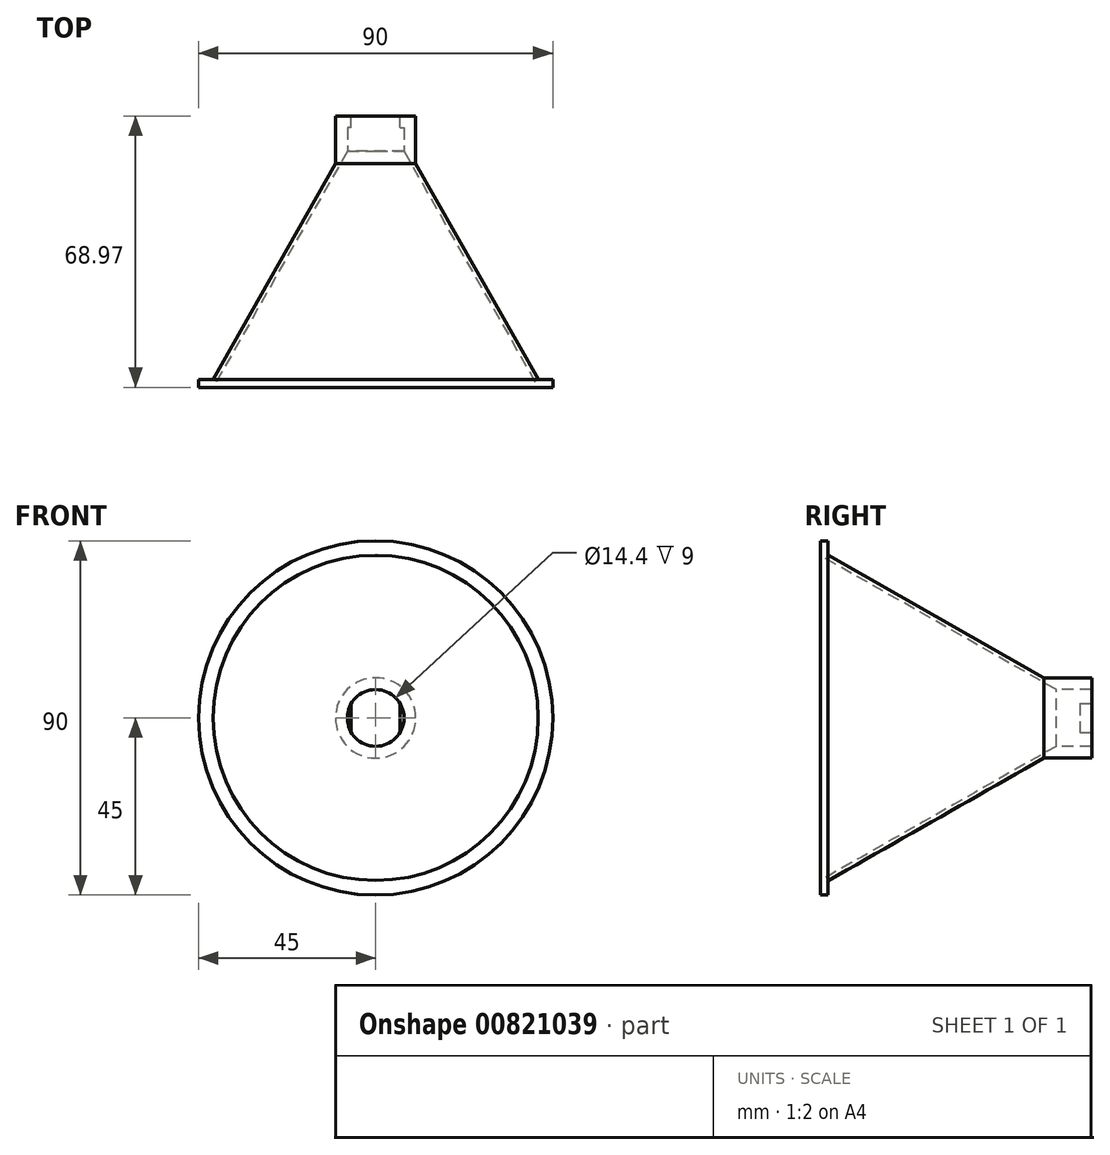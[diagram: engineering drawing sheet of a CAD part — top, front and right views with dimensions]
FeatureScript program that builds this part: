
annotation { "Feature Type Name" : "Feature", "Feature Type Description" : "" }
export const myFeature = defineFeature(function(context is Context, id is Id, definition is map)
    precondition{}
    {
        {
            var Q0;
            Q0=qCreatedBy(makeId("Top.planeOp"),FACE);
            var sketch = newSketch(context, id + "F0", { "sketchPlane" : qUnion([Q0])});
            skLineSegment(sketch, "E0", {"start": v(0, 0) * mm, "end": v(-42.5, 0) * mm});
            skLineSegment(sketch, "E1", {"start": v(0, 0) * mm, "end": v(0, 73.6) * mm});
            skLineSegment(sketch, "E2", {"start": v(0, 0) * mm, "end": v(-8.4, 0) * mm});
            skLineSegment(sketch, "E3", {"start": v(-8.4, 59.97) * mm, "end": v(0, 59.97) * mm});
            skLineSegment(sketch, "E4", {"start": v(0, 59.97) * mm, "end": v(-7.2, 59.97) * mm});
            skLineSegment(sketch, "E5", {"start": v(-8.4, 59.97) * mm, "end": v(-42.5, 0) * mm});
            skLineSegment(sketch, "E6", {"start": v(-7.2, 59.97) * mm, "end": v(-41.3, 0) * mm});
            skLineSegment(sketch, "E7", {"start": v(-7.2, 59.97) * mm, "end": v(-7.2, 68.97) * mm});
            skLineSegment(sketch, "E8", {"start": v(-7.2, 68.97) * mm, "end": v(-10.2, 68.97) * mm});
            skLineSegment(sketch, "E9", {"start": v(-10.2, 68.97) * mm, "end": v(-10.2, 59.97) * mm});
            skLineSegment(sketch, "E10", {"start": v(-10.2, 59.97) * mm, "end": v(-7.2, 59.97) * mm});
            skLineSegment(sketch, "E11", {"start": v(-10.2, 59.97) * mm, "end": v(-10.2, 56.8) * mm});
            skLineSegment(sketch, "E12", {"start": v(0, 0) * mm, "end": v(0, 2) * mm});
            skLineSegment(sketch, "E13", {"start": v(0, 2) * mm, "end": v(-45, 2) * mm});
            skLineSegment(sketch, "E14", {"start": v(-45, 2) * mm, "end": v(-45, 0) * mm});
            skLineSegment(sketch, "E15", {"start": v(-45, 0) * mm, "end": v(-42.5, 0) * mm});
            skSolve(sketch);
        }
        {
            var Q0;
            {var subQ0=sQuery(id+"F0.wireOp",EDGE,"E5");Q0=makeQuery(id+"F0.imprint","IMPRINT",FACE,{"disambiguationData":[TD([[makeQuery(id+"F0.imprint","IMPRINT",EDGE,{"derivedFrom":subQ0}),1.0]])]});}
            var Q1;
            {var subQ3=sQuery(id+"F0.wireOp",EDGE,"E11");Q1=makeQuery(id+"F0.imprint","IMPRINT",FACE,{"disambiguationData":[TD([[makeQuery(id+"F0.imprint","IMPRINT",EDGE,{"derivedFrom":subQ3}),1.0]])]});}
            var Q2;
            {var subQ3=sQuery(id+"F0.wireOp",EDGE,"E7");Q2=makeQuery(id+"F0.imprint","IMPRINT",FACE,{"disambiguationData":[TD([[makeQuery(id+"F0.imprint","IMPRINT",EDGE,{"derivedFrom":subQ3}),1.0]])]});}
            var Q3;
            {var subQ1=sQuery(id+"F0.wireOp",EDGE,"E0");var subQ3=sQuery(id+"F0.wireOp",EDGE,"E6");var subQ4=makeQuery(id+"F0.imprint","INTERSECT",VERTEX,{"derivedFrom":[subQ1,subQ3]});Q3=makeQuery(id+"F0.imprint","IMPRINT",FACE,{"disambiguationData":[TD([[makeQuery(id+"F0.imprint","IMPRINT",EDGE,{"disambiguationData":[TD([[subQ4,1.0]])],"derivedFrom":subQ3}),-1.0]])]});}
            var Q4;
            {var subQ4=sQuery(id+"F0.wireOp",EDGE,"E14");Q4=makeQuery(id+"F0.imprint","IMPRINT",FACE,{"disambiguationData":[TD([[makeQuery(id+"F0.imprint","IMPRINT",EDGE,{"derivedFrom":subQ4}),1.0]])]});}
            var Q5;
            Q5=sQuery(id+"F0.wireOp",EDGE,"E1");
            revolve(context, id + "F1", {"surfaceOperationType" : NewSurfaceOperationType.NEW, "entities" : qUnion([Q0, Q1, Q2, Q3, Q4]), "axis" : qUnion([Q5]), "revolveType" : RevolveType.FULL});
        }
        {
            var Q0;
            Q0=makeQuery(id+"F1.opRevolve","SWEPT_FACE",FACE,{"disambiguationData":[OSD([sQuery(id+"F0.wireOp",EDGE,"E8")])]});
            cPlane(context, id + "F2", {"entities" : qUnion([Q0]), "cplaneType" : CPlaneType.OFFSET, "offset" : 0 * mm, "width" : 150 * mm, "height" : 150 * mm});
        }
        {
            var Q0;
            Q0=qCreatedBy(id+"F2.planeOp",FACE);
            var sketch = newSketch(context, id + "F3", { "sketchPlane" : qUnion([Q0])});
            skCircle(sketch, "E16", {"center": v(0, 0) * mm, "radius": 7.2 * mm});
            skLineSegment(sketch, "E17", {"start": v(0, 0) * mm, "end": v(6.2, 0) * mm});
            skLineSegment(sketch, "E18", {"start": v(6.2, 3.66) * mm, "end": v(6.2, -3.66) * mm});
            skLineSegment(sketch, "E19.MirrorCS", {"start": v(-6.2, 3.66) * mm, "end": v(-6.2, -3.66) * mm});
            skSolve(sketch);
        }
        {
            var Q0;
            {var subQ0=sQuery(id+"F3.wireOp",EDGE,"E19.MirrorCS");Q0=makeQuery(id+"F3.imprint","IMPRINT",FACE,{"disambiguationData":[TD([[makeQuery(id+"F3.imprint","IMPRINT",EDGE,{"derivedFrom":subQ0}),-1.0]])]});}
            var Q1;
            {var subQ0=sQuery(id+"F3.wireOp",EDGE,"E18");var subQ4=makeQuery(id+"F3.imprint","IMPRINT",VERTEX,{"derivedFrom":subQ0});Q1=makeQuery(id+"F3.imprint","IMPRINT",FACE,{"disambiguationData":[TD([[makeQuery(id+"F3.imprint","IMPRINT",EDGE,{"disambiguationData":[TD([[subQ4,1.0]])],"derivedFrom":subQ0}),1.0]])]});}
            extrude(context, id + "F4", {"entities" : qUnion([Q0, Q1]), "operationType" : NewBodyOperationType.ADD, "oppositeDirection" : true, "depth" : 3 * mm, "offsetDistance" : 25 * mm});
        }
    });
